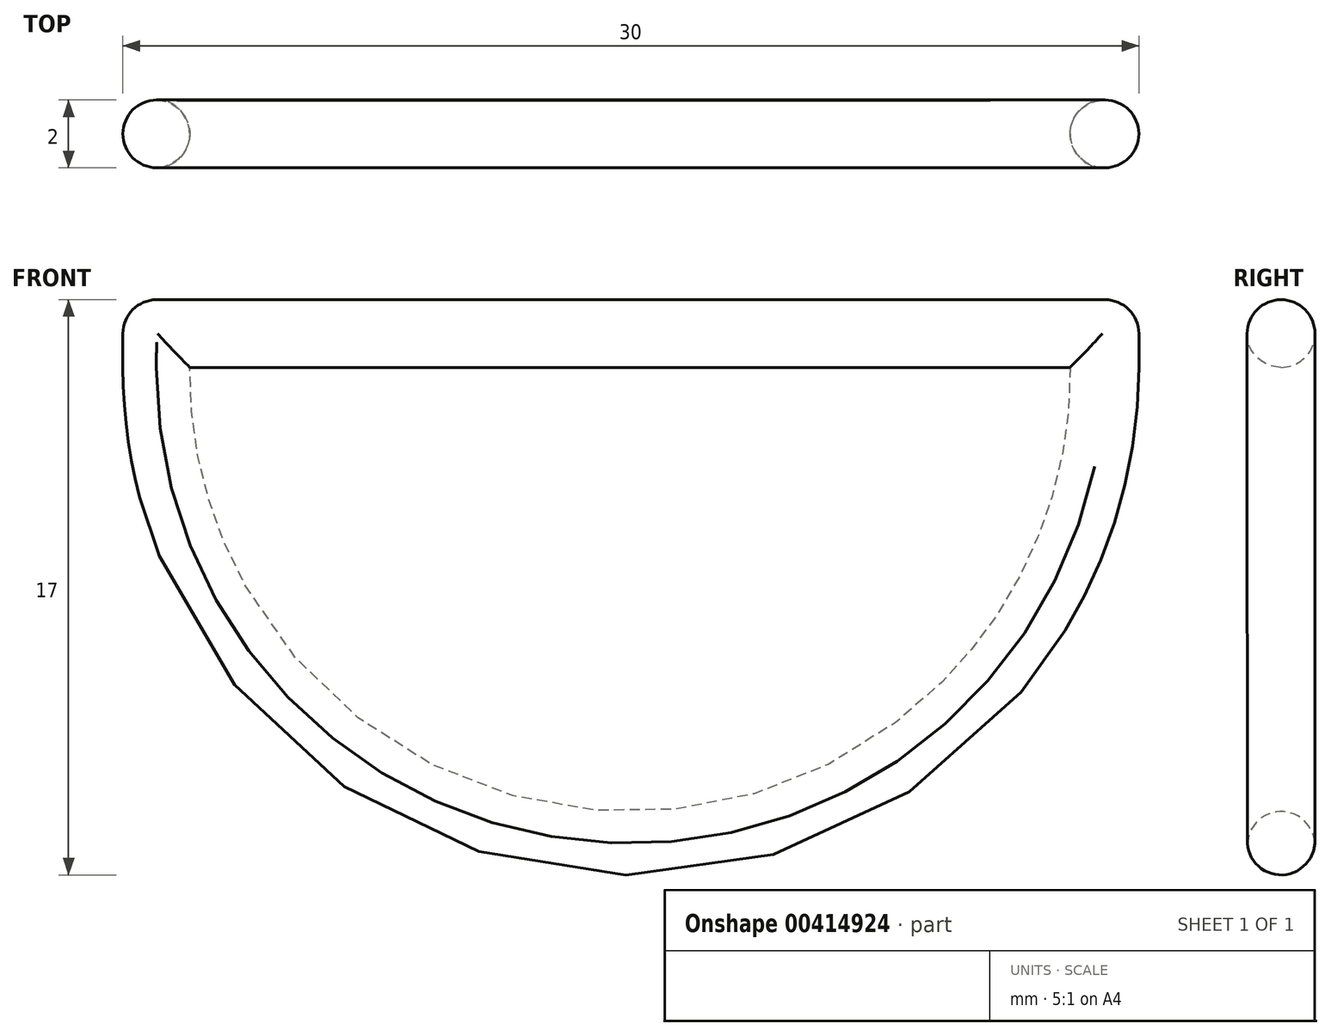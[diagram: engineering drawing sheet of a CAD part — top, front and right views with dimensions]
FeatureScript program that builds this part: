
annotation { "Feature Type Name" : "Feature", "Feature Type Description" : "" }
export const myFeature = defineFeature(function(context is Context, id is Id, definition is map)
    precondition{}
    {
        {
            var Q0;
            Q0=qCreatedBy(makeId("Front.planeOp"),FACE);
            var sketch = newSketch(context, id + "F0", { "sketchPlane" : qUnion([Q0])});
            skArc(sketch, "E0", {"start": v(-15, 0) * mm, "mid": v(0, -15) * mm, "end": v(15, 0) * mm});
            skLineSegment(sketch, "E1.0", {"start": v(-13.03, 0) * mm, "end": v(12.97, 0) * mm});
            skArc(sketch, "E1.1", {"start": v(-13.03, 0) * mm, "mid": v(-0.03, -13.13) * mm, "end": v(12.97, 0) * mm});
            skLineSegment(sketch, "E2", {"start": v(15, 0) * mm, "end": v(15, 2) * mm});
            skLineSegment(sketch, "E3", {"start": v(15, 2) * mm, "end": v(-15, 2) * mm});
            skLineSegment(sketch, "E4", {"start": v(-15, 2) * mm, "end": v(-15, 0) * mm});
            skSolve(sketch);
        }
        {
            var Q0;
            Q0=makeQuery(id+"F0.imprint","IMPRINT",FACE,{"disambiguationData":[TD([[makeQuery(id+"F0.imprint","IMPRINT",EDGE,{"derivedFrom":sQuery(id+"F0.wireOp",EDGE,"E0")}),1.0]])]});
            extrude(context, id + "F1", {"entities" : qUnion([Q0]), "endBound" : BoundingType.SYMMETRIC, "depth" : 2 * mm});
        }
        {
            var Q0;
            Q0=makeQuery(id+"F1.opExtrude","CAP_EDGE",EDGE,{"disambiguationData":[OSD([sQuery(id+"F0.wireOp",EDGE,"7Fxc6TlA-pMHv-AUk6-MQZV-DxeVgwOjDrCd")])],"isStart":false});
            var Q1;
            Q1=makeQuery(id+"F1.opExtrude","CAP_EDGE",EDGE,{"disambiguationData":[OSD([sQuery(id+"F0.wireOp",EDGE,"E1.0")])],"isStart":false});
            var Q2;
            Q2=makeQuery(id+"F1.opExtrude","CAP_EDGE",EDGE,{"disambiguationData":[OSD([sQuery(id+"F0.wireOp",EDGE,"E0")])],"isStart":false});
            var Q3;
            Q3=makeQuery(id+"F1.opExtrude","CAP_EDGE",EDGE,{"disambiguationData":[OSD([sQuery(id+"F0.wireOp",EDGE,"E1.1")])],"isStart":false});
            var Q4;
            Q4=makeQuery(id+"F1.opExtrude","CAP_EDGE",EDGE,{"disambiguationData":[OSD([sQuery(id+"F0.wireOp",EDGE,"7Fxc6TlA-pMHv-AUk6-MQZV-DxeVgwOjDrCd")])],"isStart":true});
            var Q5;
            Q5=makeQuery(id+"F1.opExtrude","CAP_EDGE",EDGE,{"disambiguationData":[OSD([sQuery(id+"F0.wireOp",EDGE,"E1.0")])],"isStart":true});
            var Q6;
            Q6=makeQuery(id+"F1.opExtrude","CAP_EDGE",EDGE,{"disambiguationData":[OSD([sQuery(id+"F0.wireOp",EDGE,"E0")])],"isStart":true});
            var Q7;
            Q7=makeQuery(id+"F1.opExtrude","CAP_EDGE",EDGE,{"disambiguationData":[OSD([sQuery(id+"F0.wireOp",EDGE,"E1.1")])],"isStart":true});
            fillet(context, id + "F2", {"entities" : qUnion([Q0, Q1, Q2, Q3, Q4, Q5, Q6, Q7]), "radius" : 1 * mm, "tangentPropagation" : true, "allowEdgeOverflow" : false});
        }
        {
            var Q0;
            Q0=makeQuery(id+"F1.opExtrude","CAP_EDGE",EDGE,{"disambiguationData":[OSD([sQuery(id+"F0.wireOp",EDGE,"E3")])],"isStart":false});
            var Q1;
            Q1=makeQuery(id+"F1.opExtrude","CAP_EDGE",EDGE,{"disambiguationData":[OSD([sQuery(id+"F0.wireOp",EDGE,"E3")])],"isStart":true});
            fillet(context, id + "F3", {"entities" : qUnion([Q0, Q1]), "radius" : 1 * mm, "tangentPropagation" : true, "allowEdgeOverflow" : false});
        }
    });
